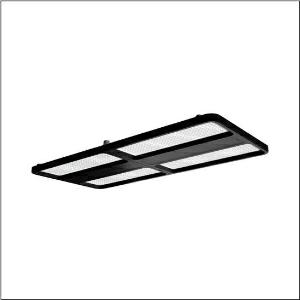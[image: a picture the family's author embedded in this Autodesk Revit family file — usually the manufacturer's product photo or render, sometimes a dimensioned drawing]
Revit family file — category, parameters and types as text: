
# Revit family: highbay_21_maxi_52hn31db4qda
name_source: partatom
category: Lighting Fixtures
units: mm (PartAtom-declared; Revit-internal decimal feet)

## family parameters
Cut with Voids When Loaded = No
Host = Face
Light Source = No
Part Type = Normal
Room Calculation Point = No
Round Connector Dimension = Use Diameter
Shared = No

## types (1)
- --- (1 x LED, 5840 lm, 31.4 W, 4000K)
    Apparent Load = 31 VA
    CIE Flux Codes = 89 97 99 100 100
    Color Rendering = 80
    Color Temperature = 4000K
    Default Elevation = 1800 mm
    Description = high bay luminaire Highbay 21 maxi; direct symmetric narrow distribution, light control with lens of PMMA; UGR ≤ 22 (X = 4H | Y = 8H | S = 0.25H | reflection values 70/50/20); luminous flux: 38.000lm; light colour: 840, colour temperature: 4000K, MacAdam ≤ 3 SDCM (initial), colour rendering: CRI > 80; luminous efficacy: 192,2lm/W; rated service life: 75.000h (L80) at AT= ta max; control: DALI 2; luminaire connection: terminal, 5-pole, max. 2.5mm² (cable entry for one cable, Ø 8.5..16mm); mains connection: 230..240V, AC/DC 0/50..60Hz; connected load: 197,7W; protection rating (complete): IP66; insulation class (complete): insulation class I (protective earthing); protection symbol: D; impact resistance: IK08; certification: CE, ENEC, VDE, UKCA; luminaire for central battery installations according to EN 60598-2-22, internal wiring halogen-free; luminaire LABS conformity tested according to VDMA 24364:2018-05; Suitable for use in the food industry according to the specifications of IFS-Food, HACCP and/or BRC; housing frame of high-performance plastic PA6, matt jet black (RAL 9005); cover of PMMA; dimension (LxWxH): 946 x 442 x 72mm; permissible operating ambient temperature: -40..+60°C (reducing of maximum allowable ambient temperature of 5°C with ceiling mounting); packaging unit: 1 piece; (delivery without accessories; please order mounting accessories separately)
    Height = 72 mm  [stored 0.23622 ft]
    Lamp = 1 x LED
    Lamp Light Flux = 5840 lm
    Lamp Power = 31.4 W
    Lamp count = 1
    Length = 946 mm
    Luminous efficacy = 186 lm/W
    Manufacturer = Siteco
    ModVariant = No
    Model = 52HN31DB4QDA
    Mounting Place = Ceiling
    Mounting Type = Pendant
    Number of Poles = 1
    OnlyDefault = Yes
    Power Factor = 1
    Product Name = Highbay 21 maxi
    Product group = high bay luminaire
    ProductGroupID = 902
    Protection Class = Protection class I
    Protection Degree = IP 66
    RLX_Detail_Level = 1
    RLX_Emergency_Light_Flux = 0 lm
    RLX_Emergency_Type = 0
    RLX_Emergency_Type_DB = No
    RlxData = <blob elided: 133709 chars, md5=0a64abbd>
    Socket = socket
    Standby Power = 0 W
    System Light Flux = 5840 lm
    System Power = 31 W
    Type Comments = : DC mode (central or group accumulator) initial emergency light level
    Type Image = l_1378821.jpg
    URL = http://relux.com
    VarID = @adj_017767
    Voltage = 0 V
    Weight = 0.00 kg
    Width = 442 mm

note: [stored X ft] marks values corroborated as IEEE doubles in the binary element streams (Revit-internal decimal feet)

## geometry (parser evidence)
native form markers: Blend x4, Sweep x10
no freeform markers — native parametric forms only
